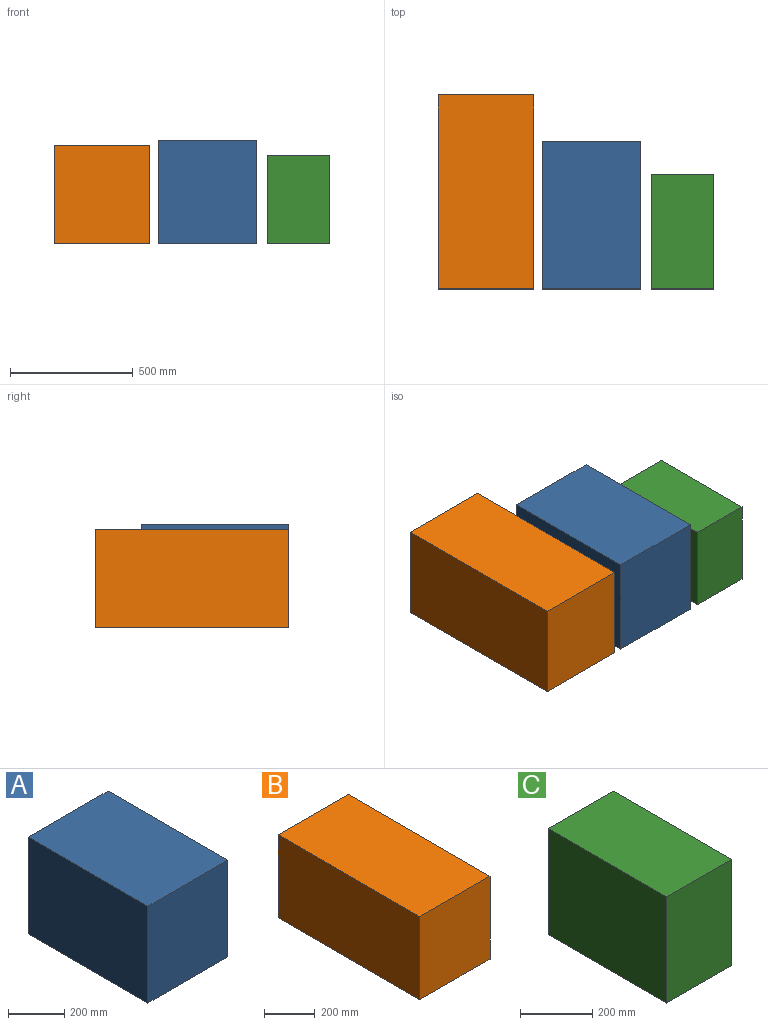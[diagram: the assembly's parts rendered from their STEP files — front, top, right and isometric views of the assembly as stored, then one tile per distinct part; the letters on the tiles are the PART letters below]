
ASSEMBLY  parts=3 mates=4
PART A: 6 faces, bbox 400x600x420 mm
  f0: plane 600x420mm, normal (-1,0,0), area 252000mm2, adj f1,f3,f4,f5
  f1: plane 600x400mm, normal (0,0,-1), area 240000mm2, adj f0,f2,f4,f5
  f2: plane 600x420mm, normal (1,0,0), area 252000mm2, adj f1,f3,f4,f5
  f3: plane 600x400mm, normal (0,0,1), area 240000mm2, adj f0,f2,f4,f5
  f4: plane 420x400mm, normal (0,-1,0), area 168000mm2, adj f0,f1,f2,f3
  f5: plane 420x400mm, normal (0,1,0), area 168000mm2, adj f0,f1,f2,f3
PART B: 6 faces, bbox 390x790x400 mm
  f0: plane 790x400mm, normal (-1,0,0), area 316000mm2, adj f1,f3,f4,f5
  f1: plane 790x390mm, normal (0,0,-1), area 308100mm2, adj f0,f2,f4,f5
  f2: plane 790x400mm, normal (1,0,0), area 316000mm2, adj f1,f3,f4,f5
  f3: plane 790x390mm, normal (0,0,1), area 308100mm2, adj f0,f2,f4,f5
  f4: plane 400x390mm, normal (0,-1,0), area 156000mm2, adj f0,f1,f2,f3
  f5: plane 400x390mm, normal (0,1,0), area 156000mm2, adj f0,f1,f2,f3
PART C: 6 faces, bbox 255x465x360 mm
  f0: plane 465x360mm, normal (-1,0,0), area 167400mm2, adj f1,f3,f4,f5
  f1: plane 465x255mm, normal (0,0,-1), area 118575mm2, adj f0,f2,f4,f5
  f2: plane 465x360mm, normal (1,0,0), area 167400mm2, adj f1,f3,f4,f5
  f3: plane 465x255mm, normal (0,0,1), area 118575mm2, adj f0,f2,f4,f5
  f4: plane 360x255mm, normal (0,-1,0), area 91800mm2, adj f0,f1,f2,f3
  f5: plane 360x255mm, normal (0,1,0), area 91800mm2, adj f0,f1,f2,f3
PLACE A t=(-94.01,131.2,-519.81)mm
PLACE B t=(-514.28,321.2,-519.81)mm
PLACE C t=(353.17,-3.8,-519.81)mm
MATE planar B.f1 <-> A.f1  axis (0,0,-1) through (-124.28,-468.8,-519.81)mm
MATE planar A.f4 <-> B.f4  axis (0,-1,0) through (109.95,-468.8,-309.81)mm
MATE planar C.f1 <-> A.f1  axis (0,0,-1) through (480.67,-236.3,-519.81)mm
MATE planar C.f4 <-> B.f4  axis (0,-1,0) through (480.67,-468.8,-339.81)mm
